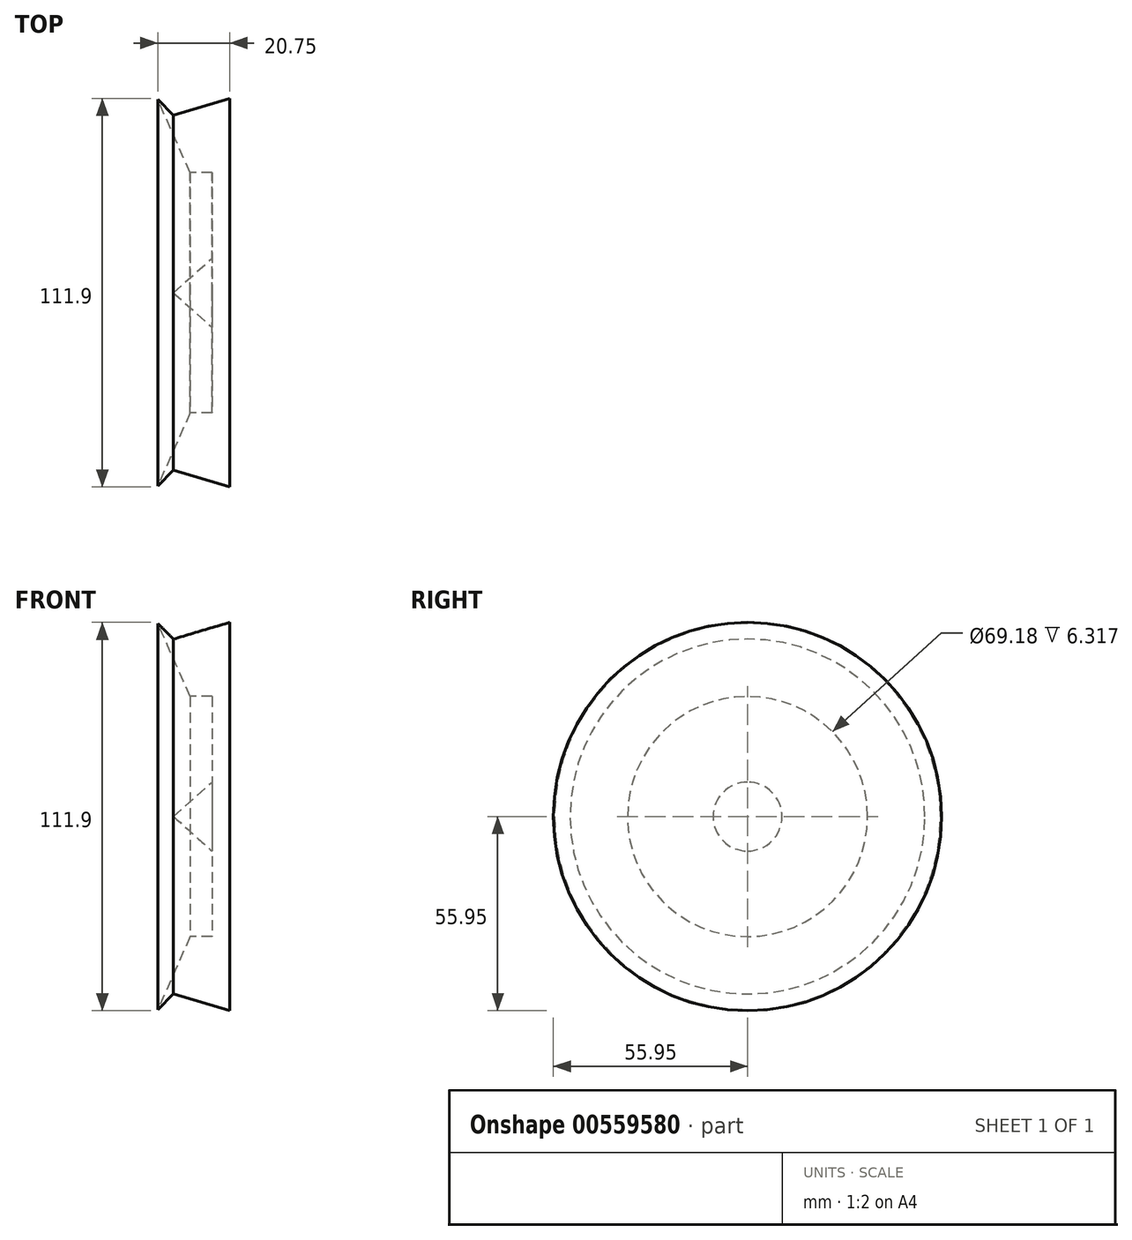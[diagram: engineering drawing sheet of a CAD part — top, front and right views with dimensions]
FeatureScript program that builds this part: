
annotation { "Feature Type Name" : "Feature", "Feature Type Description" : "" }
export const myFeature = defineFeature(function(context is Context, id is Id, definition is map)
    precondition{}
    {
        {
            var Q0;
            Q0=qCreatedBy(makeId("Front.planeOp"),FACE);
            var sketch = newSketch(context, id + "F0", { "sketchPlane" : qUnion([Q0])});
            skLineSegment(sketch, "E0", {"start": v(0, 55.95) * mm, "end": v(-16.24, 51.13) * mm});
            skLineSegment(sketch, "E1", {"start": v(-16.24, 51.13) * mm, "end": v(-20.75, 55.65) * mm});
            skLineSegment(sketch, "E2", {"start": v(-20.75, 55.65) * mm, "end": v(-11.43, 34.6) * mm});
            skLineSegment(sketch, "E3", {"start": v(-11.43, 34.6) * mm, "end": v(-5.11, 34.6) * mm});
            skLineSegment(sketch, "E4", {"start": v(-5.11, 34.6) * mm, "end": v(-5.11, 9.93) * mm});
            skLineSegment(sketch, "E5", {"start": v(-5.11, 9.93) * mm, "end": v(-16.24, 0) * mm});
            skLineSegment(sketch, "E6", {"start": v(-16.24, 0) * mm, "end": v(0, 0) * mm});
            skLineSegment(sketch, "E7", {"start": v(0, 0) * mm, "end": v(0, 55.95) * mm});
            skSolve(sketch);
        }
        {
            var Q0;
            Q0=makeQuery(id+"F0.imprint","IMPRINT",FACE,{"disambiguationData":[TD([[makeQuery(id+"F0.imprint","IMPRINT",EDGE,{"derivedFrom":sQuery(id+"F0.wireOp",EDGE,"E0")}),1.0]])]});
            var Q1;
            Q1=sQuery(id+"F0.wireOp",EDGE,"E6");
            revolve(context, id + "F1", {"entities" : qUnion([Q0]), "axis" : qUnion([Q1]), "revolveType" : RevolveType.FULL});
        }
    });
